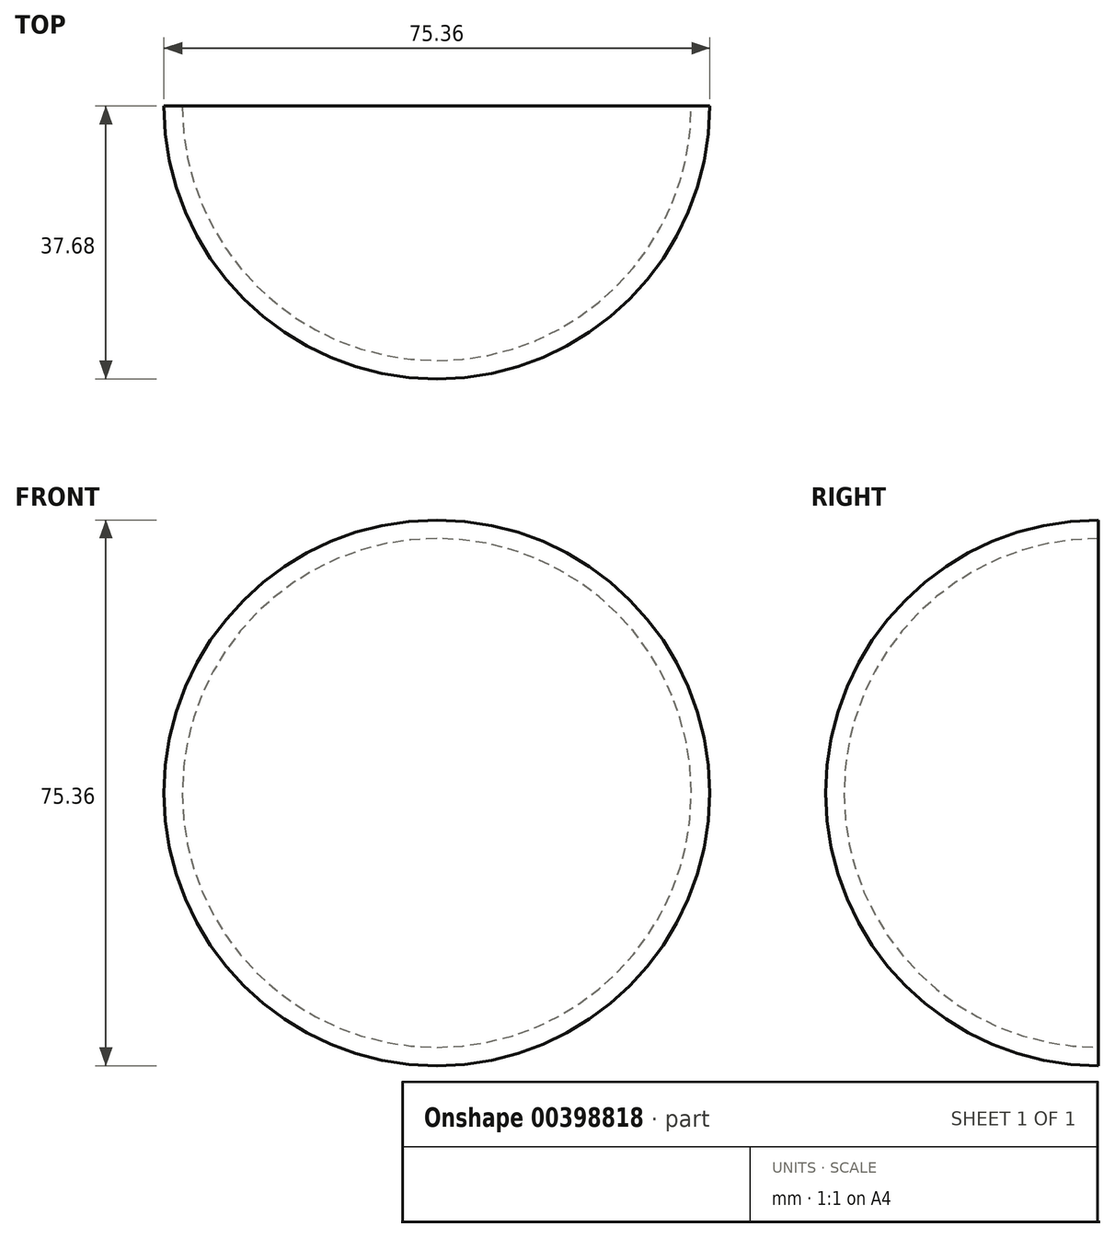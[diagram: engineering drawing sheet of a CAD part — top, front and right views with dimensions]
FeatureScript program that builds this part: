
annotation { "Feature Type Name" : "Feature", "Feature Type Description" : "" }
export const myFeature = defineFeature(function(context is Context, id is Id, definition is map)
    precondition{}
    {
        {
            var Q0;
            Q0=qCreatedBy(makeId("Front.planeOp"),FACE);
            var sketch = newSketch(context, id + "F0", { "sketchPlane" : qUnion([Q0])});
            skCircle(sketch, "E0", {"center": v(0, 0) * mm, "radius": 37.68 * mm});
            skLineSegment(sketch, "E1", {"start": v(0, 37.68) * mm, "end": v(0, -37.68) * mm});
            skSolve(sketch);
        }
        {
            var Q0;
            {var subQ0=sQuery(id+"F0.wireOp",EDGE,"E1");Q0=makeQuery(id+"F0.imprint","IMPRINT",FACE,{"disambiguationData":[TD([[makeQuery(id+"F0.imprint","IMPRINT",EDGE,{"derivedFrom":subQ0}),1.0]])]});}
            var Q1;
            Q1=sQuery(id+"F0.wireOp",EDGE,"E1");
            revolve(context, id + "F1", {"entities" : qUnion([Q0]), "axis" : qUnion([Q1]), "revolveType" : RevolveType.ONE_DIRECTION, "angle" : 180 * degree});
        }
        {
            var Q0;
            Q0=makeQuery(id+"F1.opRevolve","CAP_FACE",FACE,{"disambiguationData":[OSD([sQuery(id+"F0.wireOp",EDGE,"E0"),sQuery(id+"F0.wireOp",EDGE,"E1")])],"isStart":true});
            var Q1;
            Q1=makeQuery(id+"F1.opRevolve","CAP_FACE",FACE,{"disambiguationData":[OSD([sQuery(id+"F0.wireOp",EDGE,"E0"),sQuery(id+"F0.wireOp",EDGE,"E1")])],"isStart":false});
            shell(context, id + "F2", {"entities" : qUnion([Q0, Q1]), "thickness" : 2.54 * mm});
        }
    });
